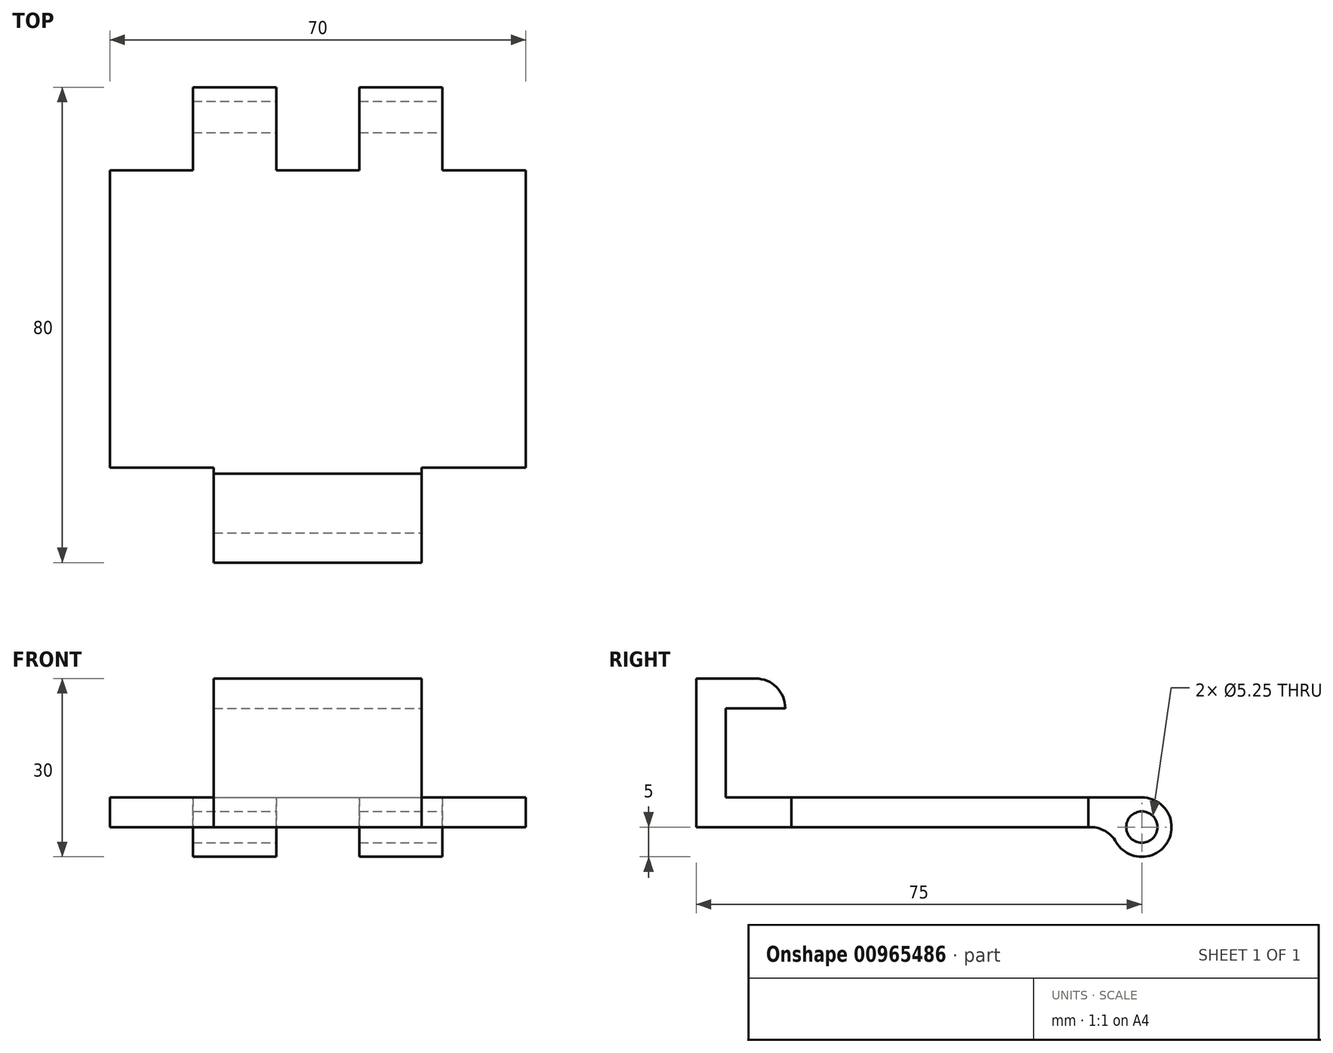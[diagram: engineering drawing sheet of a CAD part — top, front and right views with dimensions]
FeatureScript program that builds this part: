
annotation { "Feature Type Name" : "Feature", "Feature Type Description" : "" }
export const myFeature = defineFeature(function(context is Context, id is Id, definition is map)
    precondition{}
    {
        {
            var Q0;
            Q0=qCreatedBy(makeId("Right.planeOp"),FACE);
            var sketch = newSketch(context, id + "F0", { "sketchPlane" : qUnion([Q0])});
            skLineSegment(sketch, "E0", {"start": v(-20.34, 0) * mm, "end": v(0, 0) * mm, "construction": true});
            skLineSegment(sketch, "E1.0", {"start": v(-75, 14.81) * mm, "end": v(-75, 5) * mm, "construction": true});
            skLineSegment(sketch, "E2.0", {"start": v(-15, 25) * mm, "end": v(0, 25) * mm, "construction": true});
            skLineSegment(sketch, "E3.0", {"start": v(-20.34, 5) * mm, "end": v(-5, 5) * mm});
            skLineSegment(sketch, "E4", {"start": v(-20.34, 5) * mm, "end": v(-75, 5) * mm});
            skLineSegment(sketch, "E5", {"start": v(-66.34, 0) * mm, "end": v(0, 0) * mm});
            skLineSegment(sketch, "E6", {"start": v(0, 25) * mm, "end": v(-15, 25) * mm});
            skLineSegment(sketch, "E7", {"start": v(-15, 25) * mm, "end": v(-15, 20) * mm});
            skLineSegment(sketch, "E8", {"start": v(-15, 20) * mm, "end": v(-5, 20) * mm});
            skLineSegment(sketch, "E9", {"start": v(-5, 20) * mm, "end": v(-5, 5) * mm});
            skPoint(sketch, "E10.orphan", {"position": v(0, 14.81) * mm});
            skPoint(sketch, "E11.orphan", {"position": v(20.06, 25) * mm});
            skPoint(sketch, "E12.orphan", {"position": v(-20.06, 25) * mm});
            skLineSegment(sketch, "E13", {"start": v(0, 25) * mm, "end": v(0, 5) * mm});
            skLineSegment(sketch, "E14", {"start": v(0, 5) * mm, "end": v(0, 0) * mm});
            skArc(sketch, "E15", {"start": v(-75, 5) * mm, "mid": v(-79.33, -2.5) * mm, "end": v(-70.67, -2.5) * mm});
            skLineSegment(sketch, "E16.trimOffspring", {"start": v(-75, 0) * mm, "end": v(-75, -12.94) * mm, "construction": true});
            skCircle(sketch, "E17", {"center": v(-75, 0) * mm, "radius": 2.62 * mm});
            skPoint(sketch, "E18.visualSharp", {"position": v(-70, 0) * mm});
            skArc(sketch, "E18.filletArc", {"start": v(-66.34, 0) * mm, "mid": v(-68.84, -0.67) * mm, "end": v(-70.67, -2.5) * mm});
            skSolve(sketch);
        }
        {
            var Q0;
            Q0=makeQuery(id+"F0.imprint","IMPRINT",FACE,{"disambiguationData":[TD([[makeQuery(id+"F0.imprint","IMPRINT",EDGE,{"derivedFrom":sQuery(id+"F0.wireOp",EDGE,"E3.0")}),-1.0]])]});
            extrude(context, id + "F1", {"entities" : qUnion([Q0]), "depth" : 70 * mm, "offsetDistance" : 25 * mm});
        }
        {
            var Q0;
            Q0=qCreatedBy(makeId("Front.planeOp"),FACE);
            var sketch = newSketch(context, id + "F2", { "sketchPlane" : qUnion([Q0])});
            skLineSegment(sketch, "E19", {"start": v(0, 0) * mm, "end": v(0, 33.65) * mm, "construction": true});
            skLineSegment(sketch, "E20", {"start": v(0, 0) * mm, "end": v(85.21, 0) * mm, "construction": true});
            skLineSegment(sketch, "E21.0", {"start": v(17.5, 0) * mm, "end": v(17.5, 33.65) * mm, "construction": true});
            skLineSegment(sketch, "E22.0", {"start": v(0, 5) * mm, "end": v(85.21, 5) * mm, "construction": true});
            skLineSegment(sketch, "E23.left", {"start": v(17.5, 0) * mm, "end": v(17.5, 25) * mm});
            skLineSegment(sketch, "E23.right", {"start": v(52.5, 0) * mm, "end": v(52.5, 25) * mm});
            skLineSegment(sketch, "E24.bottom", {"start": v(52.5, 25) * mm, "end": v(70, 25) * mm});
            skLineSegment(sketch, "E24.top", {"start": v(52.5, 0) * mm, "end": v(70, 0) * mm});
            skLineSegment(sketch, "E24.left", {"start": v(52.5, 25) * mm, "end": v(52.5, 0) * mm});
            skLineSegment(sketch, "E24.right", {"start": v(70, 25) * mm, "end": v(70, 0) * mm});
            skLineSegment(sketch, "E25.bottom", {"start": v(17.5, 25) * mm, "end": v(0, 25) * mm});
            skLineSegment(sketch, "E25.top", {"start": v(17.5, 0) * mm, "end": v(0, 0) * mm});
            skLineSegment(sketch, "E25.left", {"start": v(17.5, 25) * mm, "end": v(17.5, 0) * mm});
            skLineSegment(sketch, "E25.right", {"start": v(0, 25) * mm, "end": v(0, 0) * mm});
            skSolve(sketch);
        }
        {
            var Q0;
            Q0=qSketchRegion(id+"F2",true);
            extrude(context, id + "F3", {"entities" : qUnion([Q0]), "operationType" : NewBodyOperationType.REMOVE, "depth" : 16 * mm, "offsetDistance" : 25 * mm});
        }
        {
            var Q0;
            Q0=qCreatedBy(makeId("Front.planeOp"),FACE);
            cPlane(context, id + "F4", {"entities" : qUnion([Q0]), "cplaneType" : CPlaneType.OFFSET, "offset" : 75 * mm, "width" : 150 * mm, "height" : 150 * mm});
        }
        {
            var Q0;
            Q0=qCreatedBy(id+"F4.planeOp",FACE);
            var sketch = newSketch(context, id + "F5", { "sketchPlane" : qUnion([Q0])});
            skLineSegment(sketch, "E26", {"start": v(0, 31.01) * mm, "end": v(0, -27.06) * mm, "construction": true});
            skLineSegment(sketch, "E27.0", {"start": v(14, 31.01) * mm, "end": v(14, -27.06) * mm, "construction": true});
            skLineSegment(sketch, "E28.0", {"start": v(28, 31.01) * mm, "end": v(28, -27.06) * mm, "construction": true});
            skLineSegment(sketch, "E29.0", {"start": v(42, 31.01) * mm, "end": v(42, -27.06) * mm, "construction": true});
            skLineSegment(sketch, "E30.0", {"start": v(56, 31.01) * mm, "end": v(56, -27.06) * mm, "construction": true});
            skLineSegment(sketch, "E31.0", {"start": v(70, 31.01) * mm, "end": v(70, -27.06) * mm, "construction": true});
            skLineSegment(sketch, "E32.bottom", {"start": v(14, -5) * mm, "end": v(0, -5) * mm});
            skLineSegment(sketch, "E32.top", {"start": v(14, 5) * mm, "end": v(0, 5) * mm});
            skLineSegment(sketch, "E32.left", {"start": v(14, -5) * mm, "end": v(14, 5) * mm});
            skLineSegment(sketch, "E32.right", {"start": v(0, -5) * mm, "end": v(0, 5) * mm});
            skLineSegment(sketch, "E33.bottom", {"start": v(42, -5) * mm, "end": v(28, -5) * mm});
            skLineSegment(sketch, "E33.top", {"start": v(42, 5) * mm, "end": v(28, 5) * mm});
            skLineSegment(sketch, "E33.left", {"start": v(42, -5) * mm, "end": v(42, 5) * mm});
            skLineSegment(sketch, "E33.right", {"start": v(28, -5) * mm, "end": v(28, 5) * mm});
            skLineSegment(sketch, "E34.bottom", {"start": v(70, -5) * mm, "end": v(56, -5) * mm});
            skLineSegment(sketch, "E34.top", {"start": v(70, 5) * mm, "end": v(56, 5) * mm});
            skLineSegment(sketch, "E34.left", {"start": v(70, -5) * mm, "end": v(70, 5) * mm});
            skLineSegment(sketch, "E34.right", {"start": v(56, -5) * mm, "end": v(56, 5) * mm});
            skSolve(sketch);
        }
        {
            var Q0;
            Q0=qSketchRegion(id+"F5",true);
            extrude(context, id + "F6", {"entities" : qUnion([Q0]), "operationType" : NewBodyOperationType.REMOVE, "oppositeDirection" : true, "depth" : 9 * mm, "offsetDistance" : 25 * mm, "hasSecondDirection" : true, "secondDirectionBound" : SecondDirectionBoundingType.THROUGH_ALL, "secondDirectionOppositeDirection" : false, "secondDirectionDepth" : 8 * mm});
        }
        {
            var Q0;
            {var subQ0=sQuery(id+"F0.wireOp",EDGE,"E7");var subQ1=sQuery(id+"F0.wireOp",EDGE,"E6");Q0=makeQuery(id+"F3.boolean.opBoolean","SPLIT",EDGE,{"disambiguationData":[TD([makeQuery(id+"F3.opExtrude","SWEPT_FACE",FACE,{"disambiguationData":[OSD([sQuery(id+"F2.wireOp",EDGE,"E23.left")])]})])],"derivedFrom":makeQuery(id+"F1.opExtrude","SWEPT_EDGE",EDGE,{"disambiguationData":[OSD([subQ1,subQ0])]})});}
            var Q1;
            {var subQ0=sQuery(id+"F0.wireOp",EDGE,"E7");var subQ1=sQuery(id+"F0.wireOp",EDGE,"E6");Q1=makeQuery(id+"F3.boolean.opBoolean","SPLIT",EDGE,{"disambiguationData":[TD([makeQuery(id+"F3.opExtrude","SWEPT_FACE",FACE,{"disambiguationData":[OSD([sQuery(id+"F2.wireOp",EDGE,"E23.right")])]})])],"derivedFrom":makeQuery(id+"F1.opExtrude","SWEPT_EDGE",EDGE,{"disambiguationData":[OSD([subQ1,subQ0])]})});}
            fillet(context, id + "F7", {"entities" : qUnion([Q0, Q1]), "radius" : 5 * mm, "tangentPropagation" : true, "allowEdgeOverflow" : false});
        }
        {
            var Q0;
            Q0=makeQuery(id+"F1.opExtrude","SWEPT_BODY",BODY,{"disambiguationData":[OSD([sQuery(id+"F0.wireOp",EDGE,"E3.0"),sQuery(id+"F0.wireOp",EDGE,"E4"),sQuery(id+"F0.wireOp",EDGE,"E5"),sQuery(id+"F0.wireOp",EDGE,"E6"),sQuery(id+"F0.wireOp",EDGE,"E7"),sQuery(id+"F0.wireOp",EDGE,"E8"),sQuery(id+"F0.wireOp",EDGE,"E9"),sQuery(id+"F0.wireOp",EDGE,"E13"),sQuery(id+"F0.wireOp",EDGE,"E14"),sQuery(id+"F0.wireOp",EDGE,"E15"),sQuery(id+"F0.wireOp",EDGE,"E17"),sQuery(id+"F0.wireOp",EDGE,"E18.filletArc")])]});
            var Q1;
            Q1=makeQuery(id+"F6.boolean.opBoolean","INTERSECT",EDGE,{"derivedFrom":[makeQuery(id+"F1.opExtrude","SWEPT_FACE",FACE,{"disambiguationData":[OSD([sQuery(id+"F0.wireOp",EDGE,"E17")])]}),makeQuery(id+"F6.opExtrude","SWEPT_FACE",FACE,{"disambiguationData":[OSD([sQuery(id+"F5.wireOp",EDGE,"E34.right")])]})]});
            transform(context, id + "F8", {"entities" : qUnion([Q0]), "transformType" : TransformType.ROTATION, "transformAxis" : qUnion([Q1]), "angle" : 180 * degree, "makeCopy" : false});
        }
        {
            var Q0;
            Q0=makeQuery(id+"F1.opExtrude","SWEPT_BODY",BODY,{"disambiguationData":[OSD([sQuery(id+"F0.wireOp",EDGE,"E3.0"),sQuery(id+"F0.wireOp",EDGE,"E4"),sQuery(id+"F0.wireOp",EDGE,"E5"),sQuery(id+"F0.wireOp",EDGE,"E6"),sQuery(id+"F0.wireOp",EDGE,"E7"),sQuery(id+"F0.wireOp",EDGE,"E8"),sQuery(id+"F0.wireOp",EDGE,"E9"),sQuery(id+"F0.wireOp",EDGE,"E13"),sQuery(id+"F0.wireOp",EDGE,"E14"),sQuery(id+"F0.wireOp",EDGE,"E15"),sQuery(id+"F0.wireOp",EDGE,"E17"),sQuery(id+"F0.wireOp",EDGE,"E18.filletArc")])]});
            var Q1;
            Q1=makeQuery(id+"F1.opExtrude","CAP_EDGE",EDGE,{"disambiguationData":[OSD([sQuery(id+"F0.wireOp",EDGE,"E5")])],"isStart":false});
            transform(context, id + "F9", {"entities" : qUnion([Q0]), "transformType" : TransformType.ROTATION, "transformAxis" : qUnion([Q1]), "angle" : 180 * degree, "makeCopy" : false});
        }
    });
